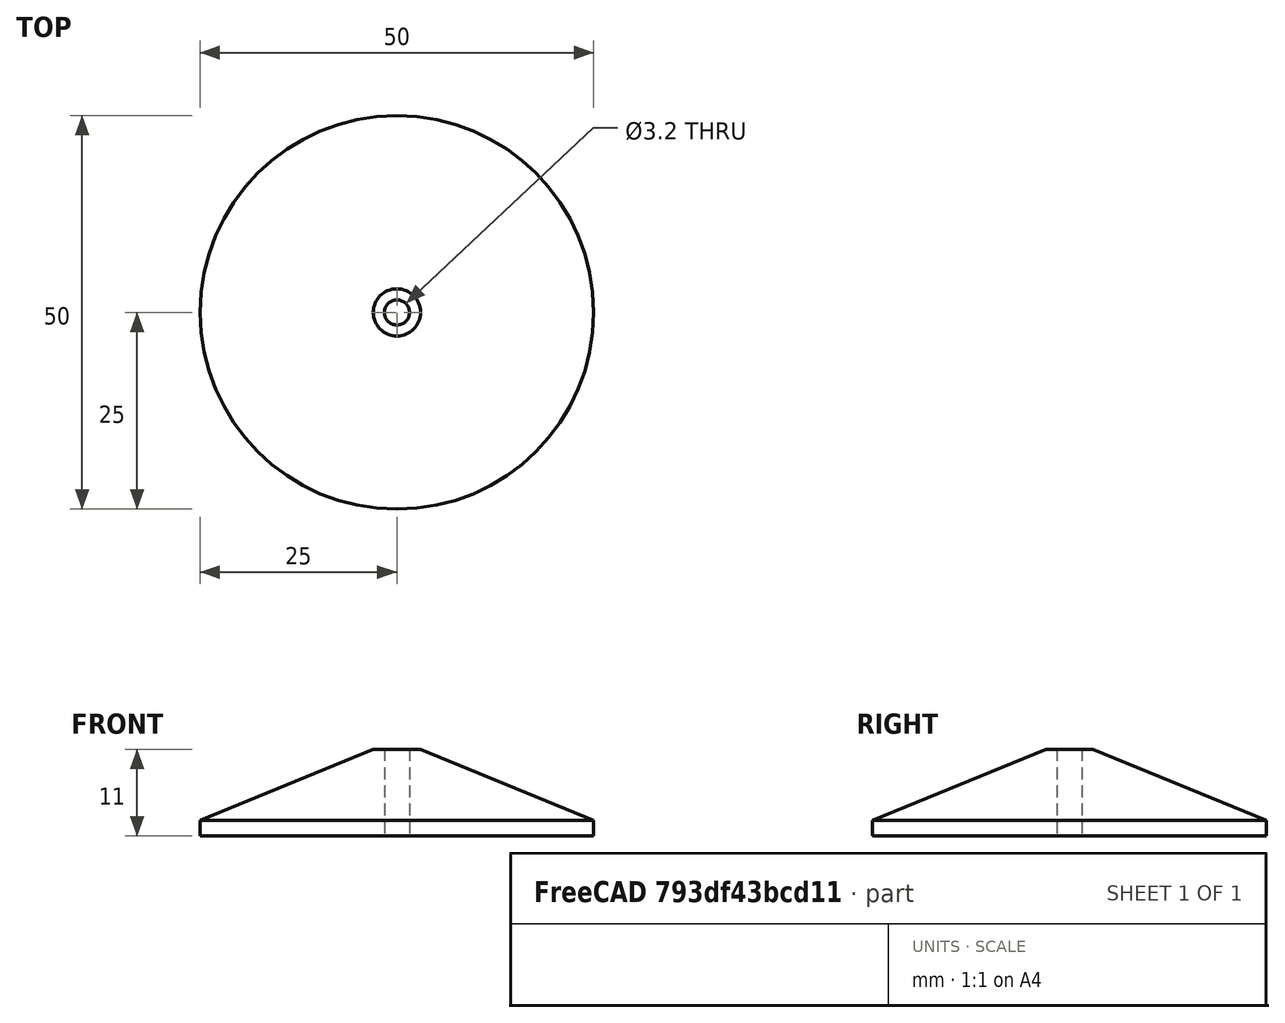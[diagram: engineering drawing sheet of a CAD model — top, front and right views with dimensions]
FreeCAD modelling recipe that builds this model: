
FCSTD DOCUMENT  (FreeCAD 0.17R13522 (Git))
Label: BobbinSocket_Big_R_A2
License: All rights reserved
LicenseURL: http://en.wikipedia.org/wiki/All_rights_reserved
objects: Sketcher::SketchObject×1, PartDesign::Revolution×1, PartDesign::Body×1, App::Part×1
note: 4 computed .brp shape members not serialized (recipe doc carries the construction recipe); baked Part::Feature solids carry a one-line shape summary decoded from their .brp

FEATURE [Sketcher::SketchObject] Sketch002
  MapMode = 5
  Placement = pos=(0,0,0) rot=(0.57735,0.57735,0.57735;2.0944rad)
  Support = -> [YZ_Plane001]
  sketch-geometry (5):
    g0: LineSegment StartX=1.6 StartY=11.0004 StartZ=0 EndX=1.6 EndY=0 EndZ=0
    g1: LineSegment StartX=25 StartY=0 StartZ=0 EndX=25 EndY=2 EndZ=0
    g2: LineSegment StartX=1.6 StartY=0 StartZ=0 EndX=25 EndY=0 EndZ=0
    g3: LineSegment StartX=1.6 StartY=11.0004 StartZ=0 EndX=3 EndY=11.0004 EndZ=0
    g4: LineSegment StartX=3 StartY=11.0004 StartZ=0 EndX=25 EndY=2 EndZ=0
  constraints (15):
    c: PointOnObject(g1,g-1)
    c: Vertical(g1)
    c: DistanceX(g-1,g0) = 1.6
    c: Vertical(g0)
    c: PointOnObject(g2,g-1)
    c: Coincident(g2,g1)
    c: DistanceX(g-1,g1) = 25
    c: Coincident(g0,g3)
    c: Horizontal(g3)
    c: Coincident(g3,g4)
    c: Coincident(g4,g1)
    c: DistanceX(g-1,g3) = 3
    c: Angle(g4,g2) = 0.388336
    c: Coincident(g2,g0)
    c: DistanceY(g1,g1) = 2
FEATURE [PartDesign::Revolution] Revolution
  Angle = 360
  Axis = (0,0,1)
  Base = (0,0,0)
  Placement = pos=(0,0,0) rot=(0.57735,0.57735,0.57735;2.0944rad)
  Profile = -> Sketch002
  ReferenceAxis = -> Sketch002 [V_Axis]
  Reversed = true
FEATURE [PartDesign::Body] RevolutionBody
  Group = -> [Sketch002,Revolution]
  Origin = -> Origin001
  Tip = -> Revolution
FEATURE [App::Part] Part
  Group = -> [RevolutionBody]
  License = CC BY 3.0
  LicenseURL = http://creativecommons.org/licenses/by/3.0/
  Origin = -> Origin
